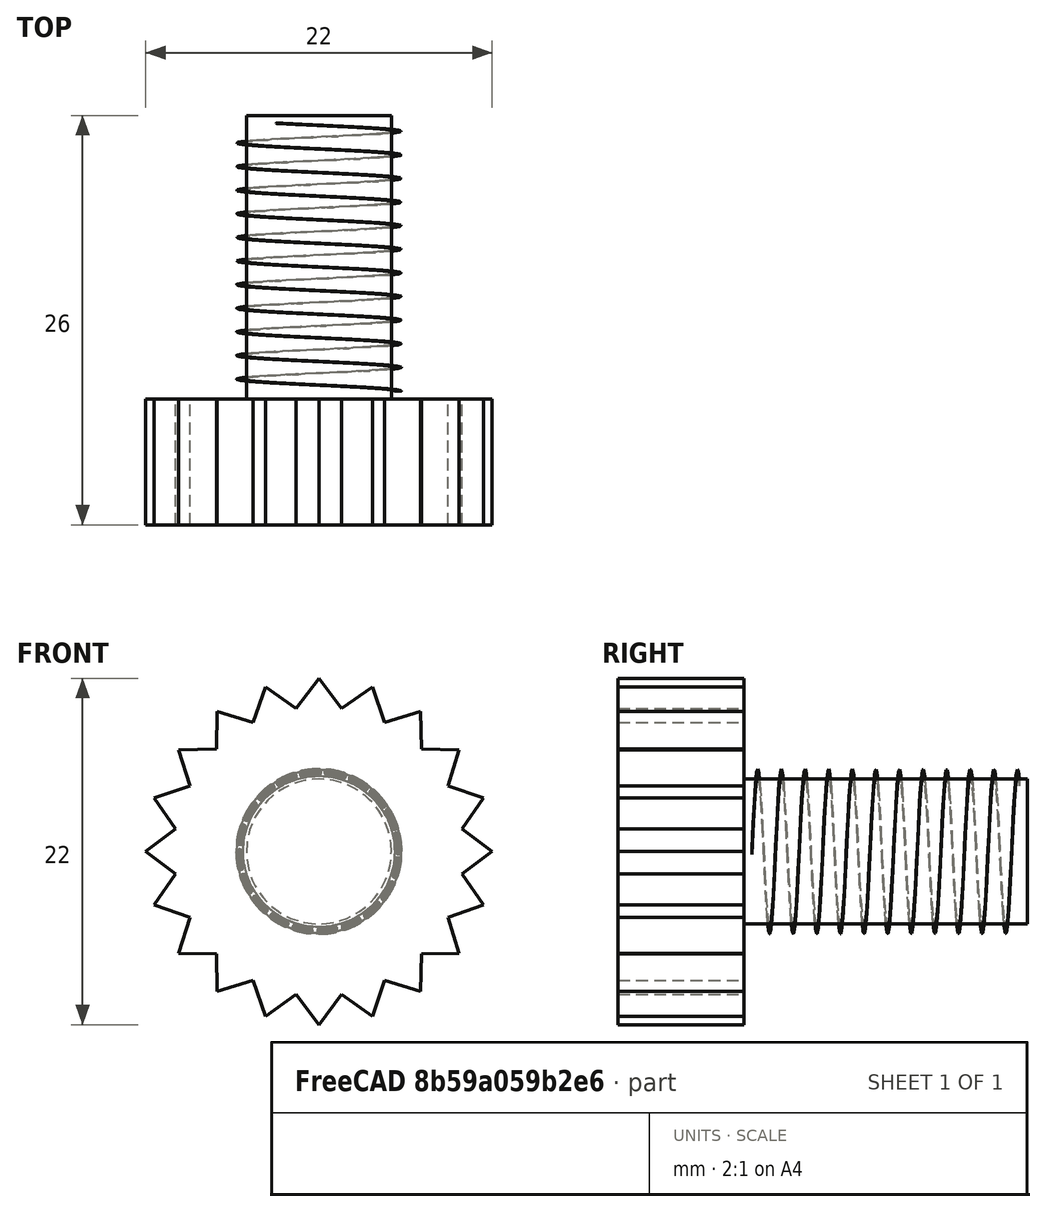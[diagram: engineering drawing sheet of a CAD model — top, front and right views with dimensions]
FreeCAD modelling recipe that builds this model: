
FCSTD DOCUMENT  (FreeCAD 1.2R20251230 (Git shallow))
Label: threaded_clamp_block_bolt
License: Creative Commons Attribution 4.0
LicenseURL: https://creativecommons.org/licenses/by/4.0/
objects: Part::Feature×3, Part::Fuse×2
note: 5 computed .brp shape members not serialized (recipe doc carries the construction recipe); baked Part::Feature solids carry a one-line shape summary decoded from their .brp

FEATURE [Part::Feature] _01_Bolt_Shaft_D9p2_L18
  shape: bbox 9.2 x 18 x 9.2 mm, 3 faces (baked)
FEATURE [Part::Feature] _02_External_Thread_Ridge
  shape: bbox 10.5 x 17 x 10.5 mm, 228 faces (baked)
FEATURE [Part::Feature] _03_Knurled_Hand_Knob
  Placement = pos=(0,-8,0) rot=(0,0,1;0rad)
  shape: bbox 22 x 8 x 22 mm, 42 faces (baked)
FEATURE [Part::Fuse] _04_Fuse_Shaft_Thread
  Base = -> _01_Bolt_Shaft_D9p2_L18
  Refine = true
  Tool = -> _02_External_Thread_Ridge
FEATURE [Part::Fuse] _05_Final_Threaded_Bolt_With_Knob
  Base = -> _04_Fuse_Shaft_Thread
  Refine = true
  Tool = -> _03_Knurled_Hand_Knob
